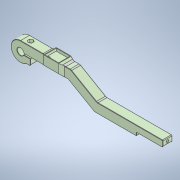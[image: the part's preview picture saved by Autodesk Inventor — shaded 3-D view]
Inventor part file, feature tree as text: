
AUTODESK INVENTOR PART (.ipt)
format: ipt  version: 2021.2 (Build 252289000, 289)  size: 424,960 bytes
history: native  units: mm
features: other x7, fillet x2, chamfer x1
ambient origin geometry x8: Origin, YZ Plane, XZ Plane, XY Plane, X Axis, Y Axis, Z Axis, Center Point
bodies: Body1 (feature_tree)
feature tree (10):
  other  "Твёрдое тело.ipt"
  fillet  "Сопряжение4"  Radius=10.0mm
  fillet  "Сопряжение5"  Radius=170.5mm
  chamfer  "Фаска3"  Distance=5.0mm
  other  "РабПлоскость2"
  other  "Разделение1"
  other  "Луч::Твёрдое тело.ipt"
  other  "Элемент создания тегов1"
  other  "РабПлоскость1"
  other  "Твердое тело1"
